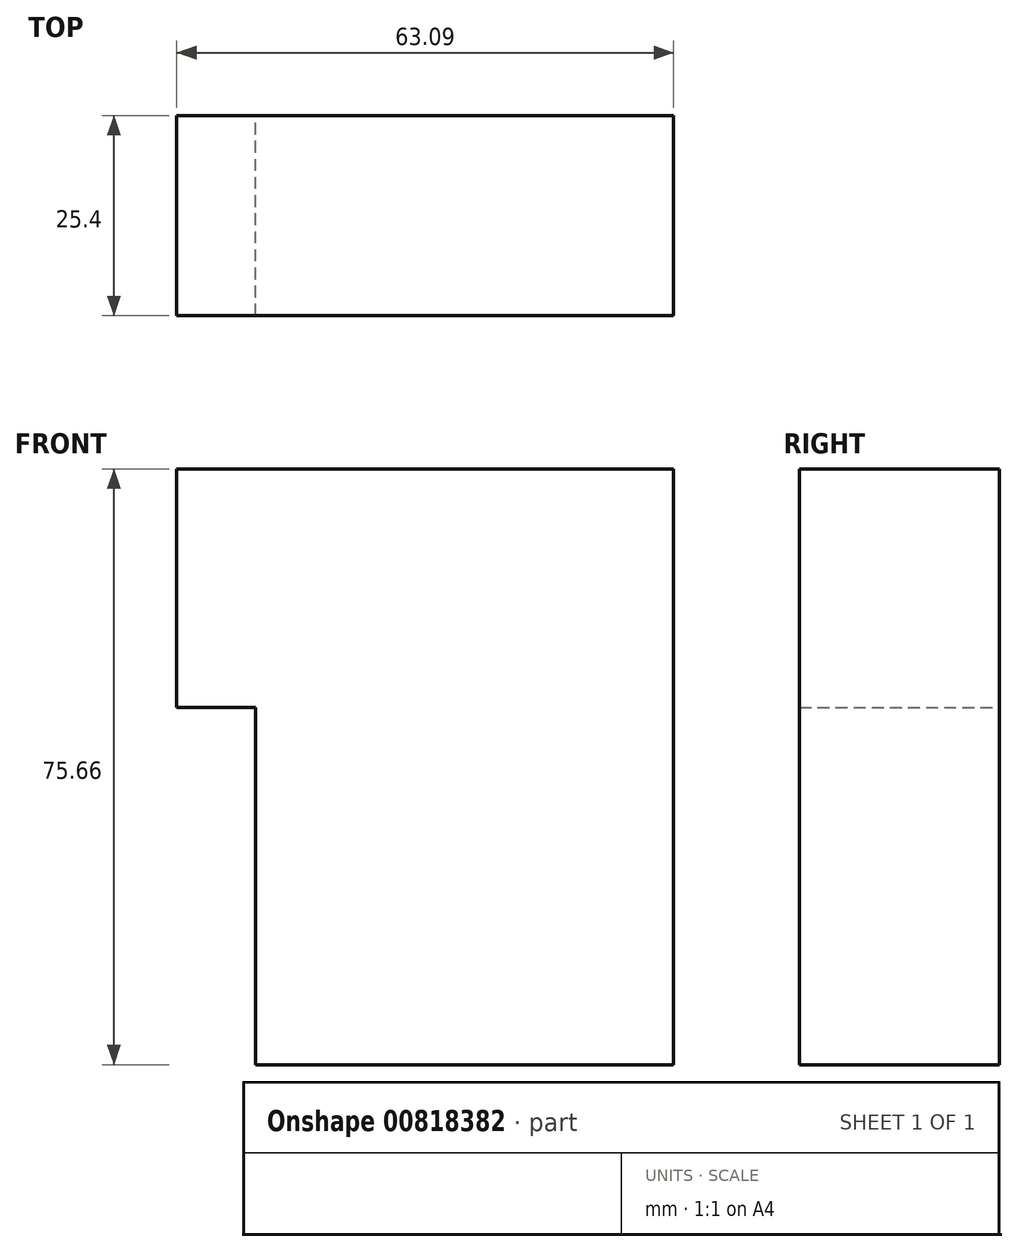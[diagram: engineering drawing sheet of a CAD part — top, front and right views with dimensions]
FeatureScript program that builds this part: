
annotation { "Feature Type Name" : "Feature", "Feature Type Description" : "" }
export const myFeature = defineFeature(function(context is Context, id is Id, definition is map)
    precondition{}
    {
        {
            var Q0;
            Q0=qCreatedBy(makeId("Front.planeOp"),FACE);
            var sketch = newSketch(context, id + "F0", { "sketchPlane" : qUnion([Q0])});
            skLineSegment(sketch, "E0.bottom", {"start": v(-109.68, 48.56) * mm, "end": v(-46.59, 48.56) * mm});
            skLineSegment(sketch, "E0.top", {"start": v(-109.68, 18.3) * mm, "end": v(-46.59, 18.3) * mm});
            skLineSegment(sketch, "E0.left", {"start": v(-109.68, 48.56) * mm, "end": v(-109.68, 18.3) * mm});
            skLineSegment(sketch, "E0.right", {"start": v(-46.59, 48.56) * mm, "end": v(-46.59, 18.3) * mm});
            skLineSegment(sketch, "E1.bottom", {"start": v(-46.59, 18.3) * mm, "end": v(-99.66, 18.3) * mm});
            skLineSegment(sketch, "E1.top", {"start": v(-46.59, -27.1) * mm, "end": v(-99.66, -27.1) * mm});
            skLineSegment(sketch, "E1.left", {"start": v(-46.59, 18.3) * mm, "end": v(-46.59, -27.1) * mm});
            skLineSegment(sketch, "E1.right", {"start": v(-99.66, 18.3) * mm, "end": v(-99.66, -27.1) * mm});
            skSolve(sketch);
        }
        {
            var Q0;
            Q0=makeQuery(id+"F0.imprint","IMPRINT",FACE,{"disambiguationData":[TD([[makeQuery(id+"F0.imprint","IMPRINT",EDGE,{"derivedFrom":sQuery(id+"F0.wireOp",EDGE,"E0.bottom")}),-1.0]])]});
            var Q1;
            Q1=makeQuery(id+"F0.imprint","IMPRINT",FACE,{"disambiguationData":[TD([[makeQuery(id+"F0.imprint","IMPRINT",EDGE,{"derivedFrom":sQuery(id+"F0.wireOp",EDGE,"E1.top")}),-1.0]])]});
            extrude(context, id + "F1", {"entities" : qUnion([Q0, Q1]), "depth" : 25.4 * mm, "offsetDistance" : 25.4 * mm});
        }
    });
